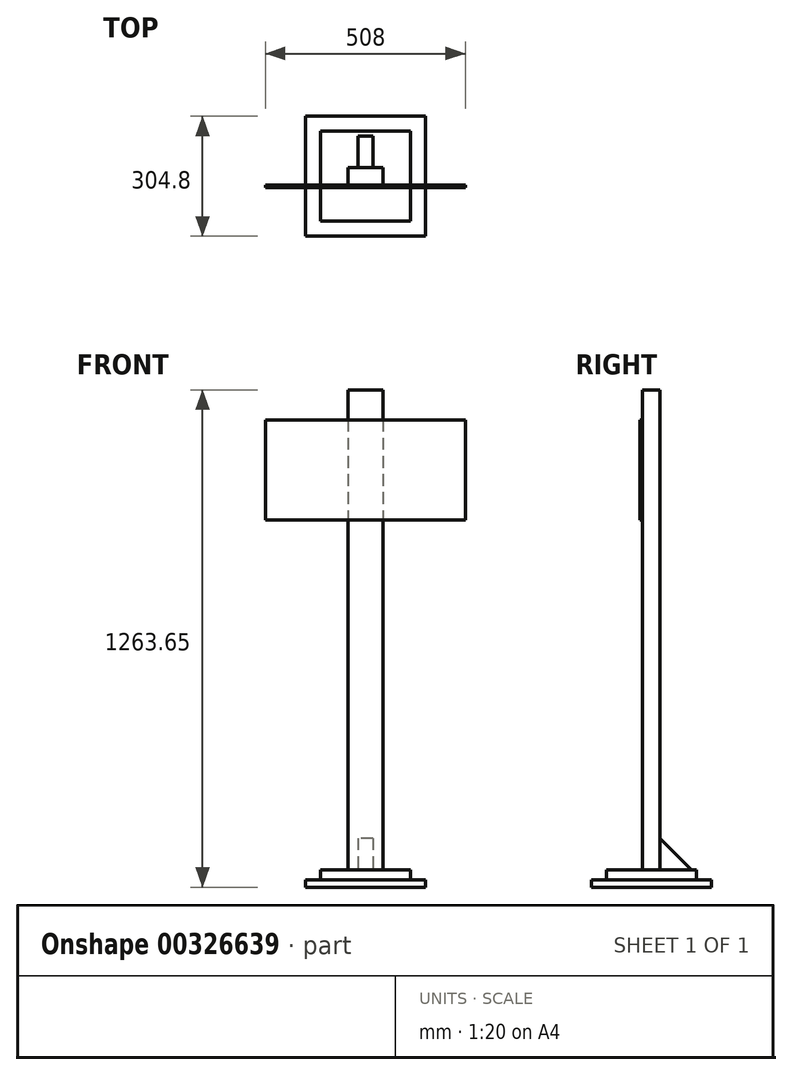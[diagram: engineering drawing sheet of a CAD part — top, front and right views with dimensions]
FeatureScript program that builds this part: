
annotation { "Feature Type Name" : "Feature", "Feature Type Description" : "" }
export const myFeature = defineFeature(function(context is Context, id is Id, definition is map)
    precondition{}
    {
        {
            var Q0;
            Q0=qCreatedBy(makeId("Top.planeOp"),FACE);
            var sketch = newSketch(context, id + "F0", { "sketchPlane" : qUnion([Q0])});
            skLineSegment(sketch, "E0.bottom", {"start": v(152.4, -152.4) * mm, "end": v(-152.4, -152.4) * mm});
            skLineSegment(sketch, "E0.top", {"start": v(152.4, 152.4) * mm, "end": v(-152.4, 152.4) * mm});
            skLineSegment(sketch, "E0.left", {"start": v(152.4, -152.4) * mm, "end": v(152.4, 152.4) * mm});
            skLineSegment(sketch, "E0.right", {"start": v(-152.4, -152.4) * mm, "end": v(-152.4, 152.4) * mm});
            skPoint(sketch, "E0.middle", {"position": v(0, 0) * mm});
            skSolve(sketch);
        }
        {
            var Q0;
            Q0 = qSketchRegion(id + "F0", true);
            extrude(context, id + "F1", {"entities" : qUnion([Q0]), "depth" : 19.05 * mm});
        }
        {
            var Q0;
            Q0=makeQuery(id+"F1.opExtrude","CAP_FACE",FACE,{"disambiguationData":[OSD([sQuery(id+"F0.wireOp",EDGE,"E0.bottom"),sQuery(id+"F0.wireOp",EDGE,"E0.top"),sQuery(id+"F0.wireOp",EDGE,"E0.left"),sQuery(id+"F0.wireOp",EDGE,"E0.right")])],"isStart":false});
            var sketch = newSketch(context, id + "F2", { "sketchPlane" : qUnion([Q0])});
            skLineSegment(sketch, "E1.bottom", {"start": v(114.3, -114.3) * mm, "end": v(-114.3, -114.3) * mm});
            skLineSegment(sketch, "E1.top", {"start": v(114.3, 114.3) * mm, "end": v(-114.3, 114.3) * mm});
            skLineSegment(sketch, "E1.left", {"start": v(114.3, -114.3) * mm, "end": v(114.3, 114.3) * mm});
            skLineSegment(sketch, "E1.right", {"start": v(-114.3, -114.3) * mm, "end": v(-114.3, 114.3) * mm});
            skPoint(sketch, "E1.middle", {"position": v(0, 0) * mm});
            skSolve(sketch);
        }
        {
            var Q0;
            Q0 = qSketchRegion(id + "F2", true);
            extrude(context, id + "F3", {"entities" : qUnion([Q0]), "operationType" : NewBodyOperationType.ADD, "depth" : 25.4 * mm});
        }
        {
            var Q0;
            Q0=makeQuery(id+"F3.opExtrude","CAP_FACE",FACE,{"disambiguationData":[OSD([sQuery(id+"F2.wireOp",EDGE,"E1.bottom"),sQuery(id+"F2.wireOp",EDGE,"E1.top"),sQuery(id+"F2.wireOp",EDGE,"E1.left"),sQuery(id+"F2.wireOp",EDGE,"E1.right")])],"isStart":false});
            var sketch = newSketch(context, id + "F4", { "sketchPlane" : qUnion([Q0])});
            skLineSegment(sketch, "E2.bottom", {"start": v(44.45, -22.22) * mm, "end": v(-44.45, -22.23) * mm});
            skLineSegment(sketch, "E2.top", {"start": v(44.45, 22.23) * mm, "end": v(-44.45, 22.22) * mm});
            skLineSegment(sketch, "E2.left", {"start": v(44.45, -22.23) * mm, "end": v(44.45, 22.23) * mm});
            skLineSegment(sketch, "E2.right", {"start": v(-44.45, -22.23) * mm, "end": v(-44.45, 22.22) * mm});
            skPoint(sketch, "E2.middle", {"position": v(0, 0) * mm});
            skSolve(sketch);
        }
        {
            var Q0;
            Q0 = qSketchRegion(id + "F4", true);
            extrude(context, id + "F5", {"entities" : qUnion([Q0]), "operationType" : NewBodyOperationType.ADD, "depth" : 1219.2 * mm});
        }
        {
            var Q0;
            Q0=makeQuery(id+"F3.opExtrude","CAP_FACE",FACE,{"disambiguationData":[OSD([sQuery(id+"F2.wireOp",EDGE,"E1.bottom"),sQuery(id+"F2.wireOp",EDGE,"E1.top"),sQuery(id+"F2.wireOp",EDGE,"E1.left"),sQuery(id+"F2.wireOp",EDGE,"E1.right")])],"isStart":false});
            var sketch = newSketch(context, id + "F6", { "sketchPlane" : qUnion([Q0])});
            skLineSegment(sketch, "E3.bottom", {"start": v(-19.05, 22.22) * mm, "end": v(19.05, 22.22) * mm});
            skLineSegment(sketch, "E3.top", {"start": v(-19.05, 101.6) * mm, "end": v(19.05, 101.6) * mm});
            skLineSegment(sketch, "E3.left", {"start": v(-19.05, 22.23) * mm, "end": v(-19.05, 101.6) * mm});
            skLineSegment(sketch, "E3.right", {"start": v(19.05, 22.23) * mm, "end": v(19.05, 101.6) * mm});
            skSolve(sketch);
        }
        {
            var Q0;
            Q0 = qSketchRegion(id + "F6", true);
            extrude(context, id + "F7", {"entities" : qUnion([Q0]), "operationType" : NewBodyOperationType.ADD, "depth" : 80 * mm});
        }
        {
            var Q0;
            Q0=makeQuery(id+"F7.opExtrude","SWEPT_FACE",FACE,{"disambiguationData":[OSD([sQuery(id+"F6.wireOp",EDGE,"E3.left")])]});
            var sketch = newSketch(context, id + "F8", { "sketchPlane" : qUnion([Q0])});
            skLineSegment(sketch, "E4", {"start": v(-101.6, 44.45) * mm, "end": v(-22.22, 124.46) * mm});
            skLineSegment(sketch, "E5", {"start": v(-22.22, 124.46) * mm, "end": v(-101.6, 124.46) * mm});
            skLineSegment(sketch, "E6", {"start": v(-101.6, 124.46) * mm, "end": v(-101.6, 44.45) * mm});
            skSolve(sketch);
        }
        {
            var Q0;
            Q0 = qSketchRegion(id + "F8", true);
            extrude(context, id + "F9", {"entities" : qUnion([Q0]), "operationType" : NewBodyOperationType.REMOVE, "oppositeDirection" : true, "depth" : 50.8 * mm});
        }
        {
            var Q0;
            Q0=makeQuery(id+"F5.opExtrude","SWEPT_FACE",FACE,{"disambiguationData":[OSD([sQuery(id+"F4.wireOp",EDGE,"E2.bottom")])]});
            var sketch = newSketch(context, id + "F10", { "sketchPlane" : qUnion([Q0])});
            skLineSegment(sketch, "E7", {"start": v(0, 1263.65) * mm, "end": v(0, 0) * mm, "construction": true});
            skLineSegment(sketch, "E8.bottom", {"start": v(254, 933.45) * mm, "end": v(-254, 933.45) * mm});
            skLineSegment(sketch, "E8.top", {"start": v(254, 1187.45) * mm, "end": v(-254, 1187.45) * mm});
            skLineSegment(sketch, "E8.left", {"start": v(254, 933.45) * mm, "end": v(254, 1187.45) * mm});
            skLineSegment(sketch, "E8.right", {"start": v(-254, 933.45) * mm, "end": v(-254, 1187.45) * mm});
            skPoint(sketch, "E8.middle", {"position": v(0, 1060.45) * mm});
            skSolve(sketch);
        }
        {
            var Q0;
            Q0 = qSketchRegion(id + "F10", true);
            extrude(context, id + "F11", {"entities" : qUnion([Q0]), "operationType" : NewBodyOperationType.ADD, "depth" : 6.35 * mm});
        }
    });
